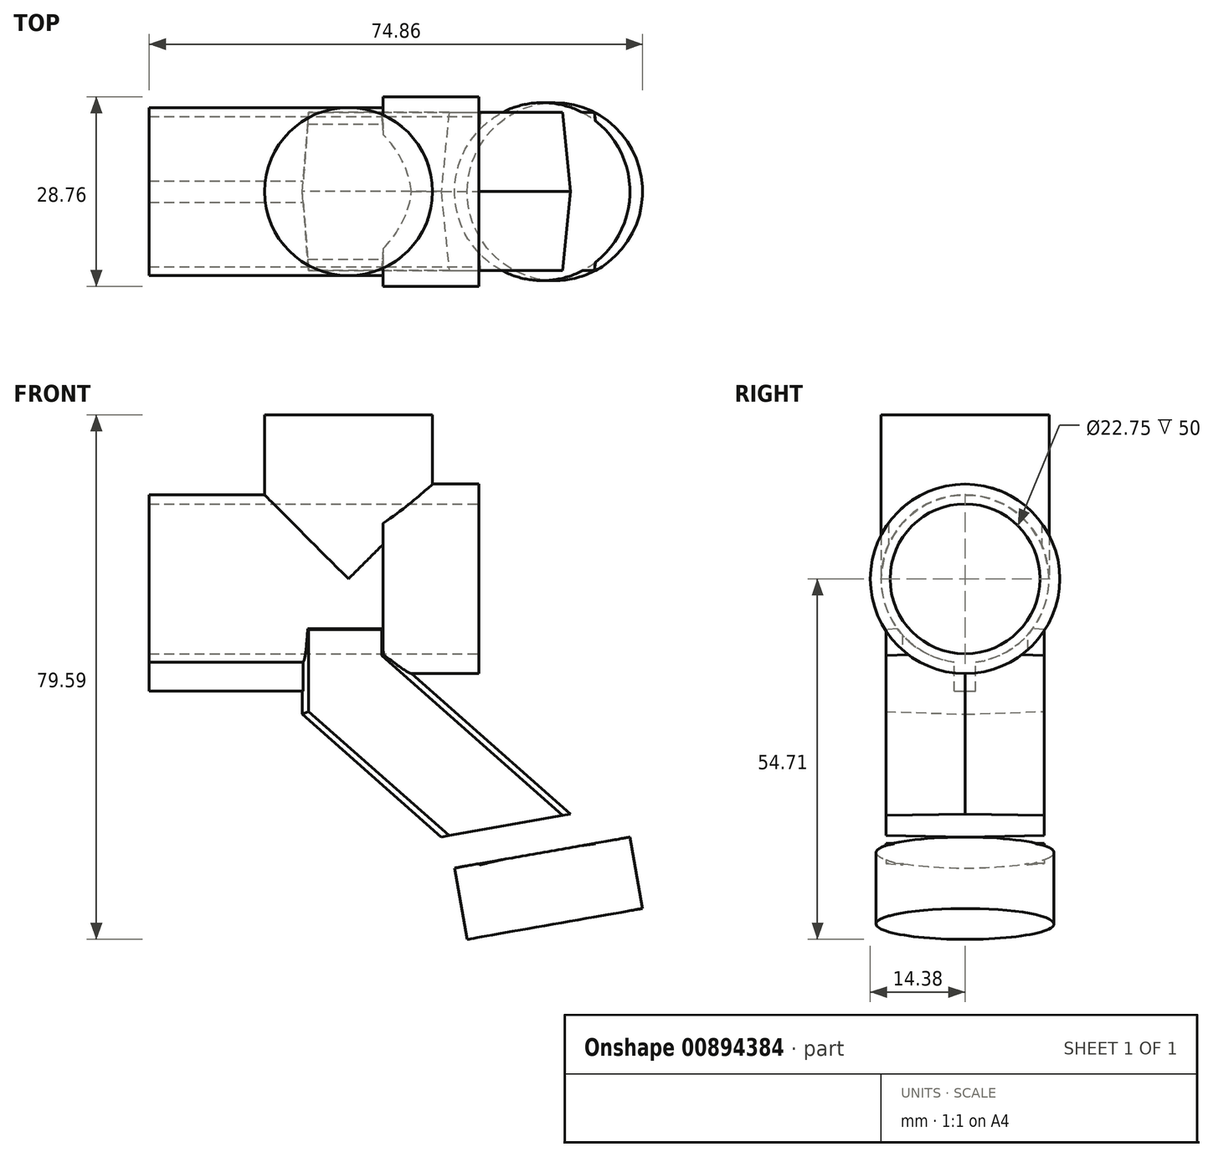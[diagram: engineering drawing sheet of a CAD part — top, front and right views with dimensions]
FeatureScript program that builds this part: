
annotation { "Feature Type Name" : "Feature", "Feature Type Description" : "" }
export const myFeature = defineFeature(function(context is Context, id is Id, definition is map)
    precondition{}
    {
        {
            var Q0;
            Q0=qCreatedBy(makeId("Right.planeOp"),FACE);
            var sketch = newSketch(context, id + "F0", { "sketchPlane" : qUnion([Q0])});
            skCircle(sketch, "E0", {"center": v(0, 0) * mm, "radius": 14.38 * mm});
            skCircle(sketch, "E1", {"center": v(0, 0) * mm, "radius": 11.38 * mm});
            skSolve(sketch);
        }
        {
            var Q0;
            Q0 = qSketchRegion(id + "F0", true);
            extrude(context, id + "F1", {"entities" : qUnion([Q0]), "oppositeDirection" : true, "depth" : 14.5 * mm, "offsetDistance" : 25 * mm});
        }
        {
            var Q0;
            Q0=makeQuery(id+"F1.opExtrude","CAP_FACE",FACE,{"disambiguationData":[OSD([sQuery(id+"F0.wireOp",EDGE,"E0"),sQuery(id+"F0.wireOp",EDGE,"E1")])],"isStart":false});
            var sketch = newSketch(context, id + "F2", { "sketchPlane" : qUnion([Q0])});
            skCircle(sketch, "E2", {"center": v(0, 0) * mm, "radius": 12.75 * mm});
            skCircle(sketch, "E3.0", {"center": v(0, 0) * mm, "radius": 11.38 * mm});
            skSolve(sketch);
        }
        {
            var Q0;
            Q0 = qSketchRegion(id + "F2", true);
            extrude(context, id + "F3", {"entities" : qUnion([Q0]), "operationType" : NewBodyOperationType.ADD, "depth" : (50 - 14.5) * mm, "offsetDistance" : 25 * mm});
        }
        {
            var Q0;
            Q0=qCreatedBy(makeId("Top.planeOp"),FACE);
            var sketch = newSketch(context, id + "F4", { "sketchPlane" : qUnion([Q0])});
            skPoint(sketch, "E4", {"position": v(-19.75, 0) * mm});
            skCircle(sketch, "E5", {"center": v(-19.75, 0) * mm, "radius": 12.75 * mm});
            skSolve(sketch);
        }
        {
            var Q0;
            Q0 = qSketchRegion(id + "F4", true);
            extrude(context, id + "F5", {"entities" : qUnion([Q0]), "operationType" : NewBodyOperationType.ADD, "depth" : 24.88 * mm, "offsetDistance" : 25 * mm});
        }
        {
            var Q0;
            Q0=qCreatedBy(makeId("Front.planeOp"),FACE);
            var sketch = newSketch(context, id + "F6", { "sketchPlane" : qUnion([Q0])});
            skLineSegment(sketch, "E6.bottom", {"start": v(-26.75, -6.75) * mm, "end": v(-13.75, -6.75) * mm});
            skLineSegment(sketch, "E6.left", {"start": v(-26.75, -6.75) * mm, "end": v(-26.75, -12.75) * mm});
            skLineSegment(sketch, "E6.right", {"start": v(-13.75, -6.75) * mm, "end": v(-13.75, -11.22) * mm});
            skLineSegment(sketch, "E7.bottom", {"start": v(-50, -12.75) * mm, "end": v(-26.75, -12.75) * mm});
            skLineSegment(sketch, "E7.top", {"start": v(-50, -17.05) * mm, "end": v(-26.75, -17.05) * mm});
            skLineSegment(sketch, "E7.left", {"start": v(-50, -12.75) * mm, "end": v(-50, -17.05) * mm});
            skLineSegment(sketch, "E8", {"start": v(-26.75, -20.55) * mm, "end": v(0, -44.2) * mm});
            skLineSegment(sketch, "E9", {"start": v(-13.75, -11.22) * mm, "end": v(19.64, -40.73) * mm});
            skPoint(sketch, "E10", {"position": v(0, -23.37) * mm});
            skLineSegment(sketch, "E11", {"start": v(0, -44.2) * mm, "end": v(19.64, -40.73) * mm});
            skLineSegment(sketch, "E12.trimOffspring", {"start": v(-26.75, -17.05) * mm, "end": v(-26.75, -20.55) * mm});
            skLineSegment(sketch, "E13", {"start": v(-26.75, -12.75) * mm, "end": v(-26.75, -17.05) * mm});
            skLineSegment(sketch, "E14.top", {"start": v(-50, -8.05) * mm, "end": v(-26.75, -8.05) * mm});
            skLineSegment(sketch, "E14.left", {"start": v(-50, -12.75) * mm, "end": v(-50, -8.05) * mm});
            skLineSegment(sketch, "E14.right", {"start": v(-26.75, -12.75) * mm, "end": v(-26.75, -8.05) * mm});
            skLineSegment(sketch, "E15", {"start": v(0, -44.2) * mm, "end": v(31.92, -44.2) * mm, "construction": true});
            skSolve(sketch);
        }
        {
            var Q0;
            Q0=makeQuery(id+"F6.imprint","IMPRINT",FACE,{"disambiguationData":[TD([[makeQuery(id+"F6.imprint","IMPRINT",EDGE,{"derivedFrom":sQuery(id+"F6.wireOp",EDGE,"E6.bottom")}),-1.0]])]});
            extrude(context, id + "F7", {"entities" : qUnion([Q0]), "operationType" : NewBodyOperationType.ADD, "depth" : (24 / 2) * mm, "offsetDistance" : 25 * mm, "hasDraft" : true, "draftAngle" : 4.5 * degree, "draftPullDirection" : true, "hasSecondDirection" : true, "secondDirectionOppositeDirection" : true, "secondDirectionDepth" : (24 / 2) * mm, "hasSecondDirectionDraft" : true, "secondDirectionDraftAngle" : 4.5 * degree, "secondDirectionDraftPullDirection" : true});
        }
        {
            var Q0;
            Q0=makeQuery(id+"F1.opExtrude","CAP_FACE",FACE,{"disambiguationData":[OSD([sQuery(id+"F0.wireOp",EDGE,"E0"),sQuery(id+"F0.wireOp",EDGE,"E1")])],"isStart":true});
            var sketch = newSketch(context, id + "F8", { "sketchPlane" : qUnion([Q0])});
            skCircle(sketch, "E16.0", {"center": v(0, 0) * mm, "radius": 11.38 * mm});
            skSolve(sketch);
        }
        {
            var Q0;
            Q0 = qSketchRegion(id + "F8", true);
            extrude(context, id + "F9", {"entities" : qUnion([Q0]), "operationType" : NewBodyOperationType.REMOVE, "endBound" : BoundingType.THROUGH_ALL, "oppositeDirection" : true, "depth" : 25 * mm, "offsetDistance" : 25 * mm});
        }
        {
            var Q0;
            Q0=qCreatedBy(makeId("Front.planeOp"),FACE);
            var sketch = newSketch(context, id + "F10", { "sketchPlane" : qUnion([Q0])});
            skLineSegment(sketch, "E17.left", {"start": v(-50, -11.38) * mm, "end": v(-50, -17.05) * mm});
            skLineSegment(sketch, "E18", {"start": v(-50, -17.05) * mm, "end": v(-23.8, -17.05) * mm});
            skLineSegment(sketch, "E19", {"start": v(-23.8, -17.05) * mm, "end": v(-23.8, -11.37) * mm});
            skLineSegment(sketch, "E20", {"start": v(-23.8, -11.37) * mm, "end": v(-50, -11.37) * mm});
            skSolve(sketch);
        }
        {
            var Q0;
            Q0 = qSketchRegion(id + "F10", true);
            extrude(context, id + "F11", {"entities" : qUnion([Q0]), "operationType" : NewBodyOperationType.ADD, "depth" : (3.25 / 2) * mm, "offsetDistance" : 25 * mm, "hasSecondDirection" : true, "secondDirectionOppositeDirection" : true, "secondDirectionDepth" : (3.25 / 2) * mm});
        }
        {
            var Q0;
            Q0=makeQuery(id+"F7.opExtrude","CAP_VERTEX",VERTEX,{"disambiguationData":[OSD([sQuery(id+"F6.wireOp",EDGE,"E8"),sQuery(id+"F6.wireOp",EDGE,"E11")])],"isStart":false});
            var Q1;
            Q1=makeQuery(id+"F7.opExtrude","CAP_VERTEX",VERTEX,{"disambiguationData":[OSD([sQuery(id+"F6.wireOp",EDGE,"E9"),sQuery(id+"F6.wireOp",EDGE,"E11")])],"isStart":false});
            var Q2;
            Q2=makeQuery(id+"F7.opExtrude","CAP_VERTEX",VERTEX,{"disambiguationData":[OSD([sQuery(id+"F6.wireOp",EDGE,"E9"),sQuery(id+"F6.wireOp",EDGE,"E11")])],"isStart":true});
            cPlane(context, id + "F12", {"entities" : qUnion([Q0, Q1, Q2]), "cplaneType" : CPlaneType.THREE_POINT, "offset" : 25 * mm, "width" : 150 * mm, "height" : 150 * mm});
        }
        {
            var Q0;
            Q0=qCreatedBy(id+"F12.planeOp",FACE);
            var sketch = newSketch(context, id + "F13", { "sketchPlane" : qUnion([Q0])});
            skCircle(sketch, "E21", {"center": v(2.3, 0) * mm, "radius": 13.5 * mm});
            skSolve(sketch);
        }
        {
            var Q0;
            Q0 = qSketchRegion(id + "F13", true);
            extrude(context, id + "F14", {"entities" : qUnion([Q0]), "operationType" : NewBodyOperationType.ADD, "depth" : 11 * mm, "offsetDistance" : 25 * mm});
        }
        {
            var Q0;
            Q0=qCreatedBy(makeId("Front.planeOp"),FACE);
            var sketch = newSketch(context, id + "F15", { "sketchPlane" : qUnion([Q0])});
            skLineSegment(sketch, "E22", {"start": v(-13.04, -45.54) * mm, "end": v(30.83, -37.8) * mm});
            skLineSegment(sketch, "E23", {"start": v(-13.91, -40.61) * mm, "end": v(29.96, -32.88) * mm});
            skLineSegment(sketch, "E24", {"start": v(30.83, -37.8) * mm, "end": v(29.96, -32.88) * mm});
            skLineSegment(sketch, "E25", {"start": v(-13.04, -45.54) * mm, "end": v(-13.91, -40.61) * mm});
            skPoint(sketch, "E26.orphan", {"position": v(-6.2, -84.4) * mm});
            skPoint(sketch, "E27.orphan", {"position": v(-6.2, -39.25) * mm});
            skSolve(sketch);
        }
        {
            var Q0;
            Q0 = qSketchRegion(id + "F15", true);
            extrude(context, id + "F16", {"entities" : qUnion([Q0]), "operationType" : NewBodyOperationType.REMOVE, "endBound" : BoundingType.THROUGH_ALL, "oppositeDirection" : true, "depth" : 25 * mm, "offsetDistance" : 25 * mm, "hasSecondDirection" : true, "secondDirectionBound" : SecondDirectionBoundingType.THROUGH_ALL, "secondDirectionOppositeDirection" : false, "secondDirectionDepth" : 25 * mm});
        }
    });
